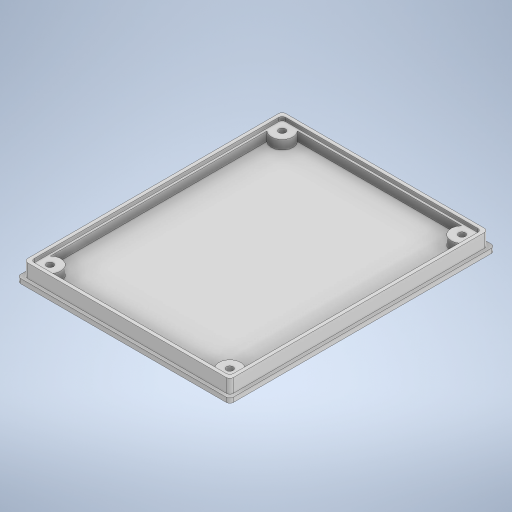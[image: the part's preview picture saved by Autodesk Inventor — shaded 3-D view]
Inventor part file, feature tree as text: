
AUTODESK INVENTOR PART (.ipt)
format: ipt  version: 2023 (Build 270158000, 158)  size: 340,480 bytes
history: native  units: in
note: dims shown in document units (in); Inventor stores cm internally (conversion verified against a paired STEP export)
features: extrude x6, sketch x6, fillet x2
ambient origin geometry x8: Origin, YZ Plane, XZ Plane, XY Plane, X Axis, Y Axis, Z Axis, Center Point
bodies: Solid1 (feature_tree)
feature tree (14):
  extrude  "Extrusion1"  Depth=3.6811in
  extrude  "Extrusion2"  Depth=4.3504in
  extrude  "Extrusion3"  Depth=0.063in TaperAngle=0.0deg
  extrude  "Extrusion4"  Depth=3.3661in
  extrude  "Extrusion5"  Depth=0.1575in
  fillet  "Fillet1"  Radius=0.374in
  extrude  "Extrusion6"  Depth=0.0591in
  fillet  "Fillet3"  Radius=3.1102in
  sketch  "Sketch1"  dims[d0=4.5866in d1=3.6811in]
  sketch  "Sketch2"  dims[d2=0.315in d3=0.0in d4=4.3504in]
  sketch  "Sketch3"  dims[d5=3.4449in d6=0.063in d7=0.0in]
  sketch  "Sketch4"  dims[d8=4.2717in d9=3.3661in]
  sketch  "Sketch5"  dims[d10=0.1575in d11=0.0in d12=0.374in d13=0.374in]
  sketch  "Sketch6"  dims[d14=4.0157in d17=0.374in d20=3.1102in d21=0.374in d22=4.0157in d23=3.1102in d25=0.1575in d26=0.0in d27=0.1181in d28=0.1181in d29=0.1181in d30=0.1181in d31=0.1575in d32=0.0in d33=0.0591in d35=4.4685in d36=3.563in d37=5.4528in d38=3.937in d39=0.2362in d40=0.0in d41=0.0591in d42=0.1673in d43=0.1673in d44=0.1673in d45=0.1673in]
